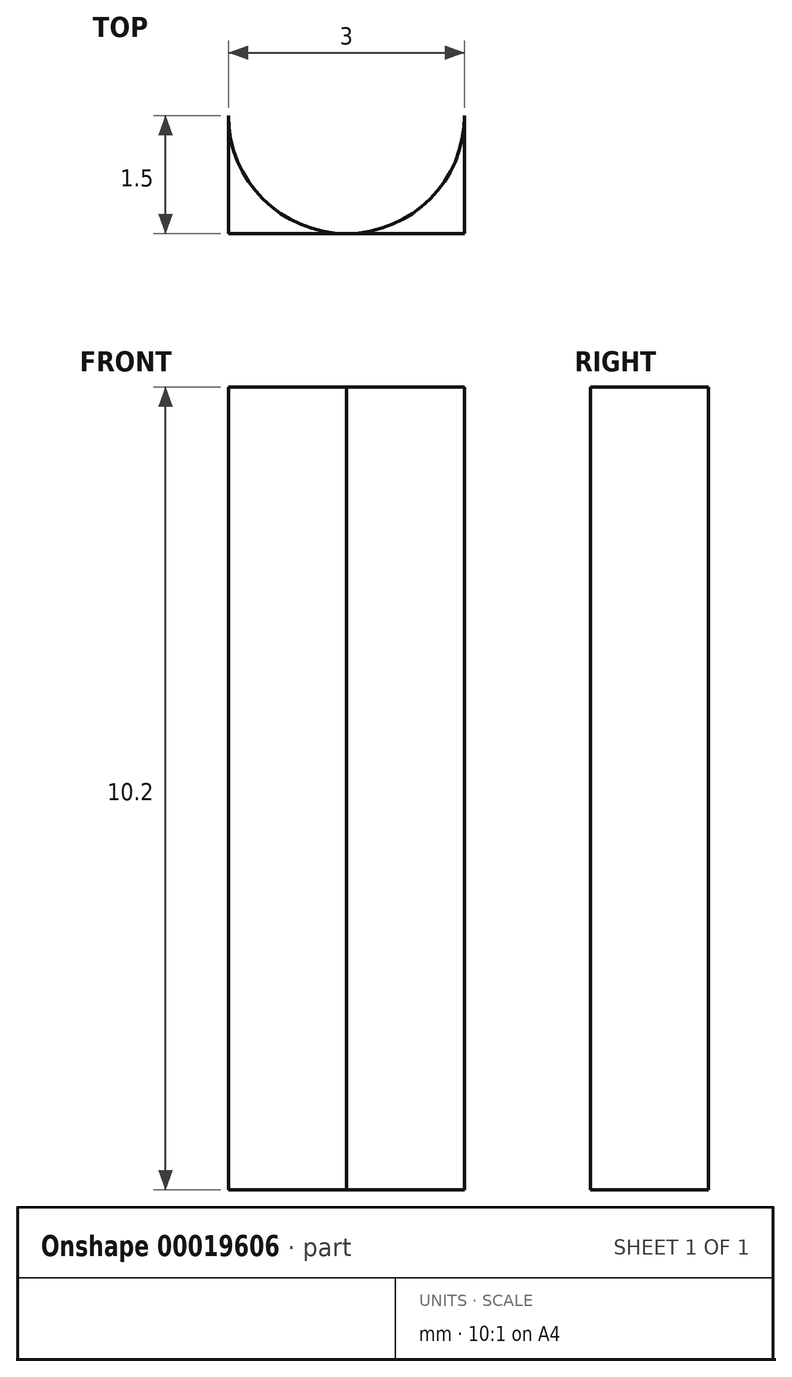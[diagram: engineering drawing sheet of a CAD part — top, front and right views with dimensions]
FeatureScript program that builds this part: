
annotation { "Feature Type Name" : "Feature", "Feature Type Description" : "" }
export const myFeature = defineFeature(function(context is Context, id is Id, definition is map)
    precondition{}
    {
        {
            var Q0;
            Q0=qCreatedBy(makeId("Top.planeOp"),FACE);
            var sketch = newSketch(context, id + "F0", { "sketchPlane" : qUnion([Q0])});
            skLineSegment(sketch, "E0.rect.top", {"start": v(-1.5, -1.5) * mm, "end": v(1.5, -1.5) * mm});
            skLineSegment(sketch, "E0.rect.left", {"start": v(-1.5, 0) * mm, "end": v(-1.5, -1.5) * mm});
            skLineSegment(sketch, "E0.rect.right", {"start": v(1.5, 0) * mm, "end": v(1.5, -1.5) * mm});
            skPoint(sketch, "E0.rect.middle", {"position": v(0, 0) * mm});
            skArc(sketch, "E1", {"start": v(-1.5, 0) * mm, "mid": v(0, -1.5) * mm, "end": v(1.5, 0) * mm});
            skPoint(sketch, "E2.orphan", {"position": v(-1.5, 1.5) * mm});
            skPoint(sketch, "E3.orphan", {"position": v(1.5, 1.5) * mm});
            skSolve(sketch);
        }
        {
            var Q0;
            {var subQ3=sQuery(id+"F0.wireOp",EDGE,"E0.rect.left");Q0=makeQuery(id+"F0.imprint","IMPRINT",FACE,{"disambiguationData":[TD([[makeQuery(id+"F0.imprint","IMPRINT",EDGE,{"derivedFrom":subQ3}),1.0]])]});}
            var Q1;
            {var subQ3=sQuery(id+"F0.wireOp",EDGE,"E0.rect.right");Q1=makeQuery(id+"F0.imprint","IMPRINT",FACE,{"disambiguationData":[TD([[makeQuery(id+"F0.imprint","IMPRINT",EDGE,{"derivedFrom":subQ3}),-1.0]])]});}
            extrude(context, id + "F1", {"entities" : qUnion([Q0, Q1]), "depth" : 10.2 * mm});
        }
    });
